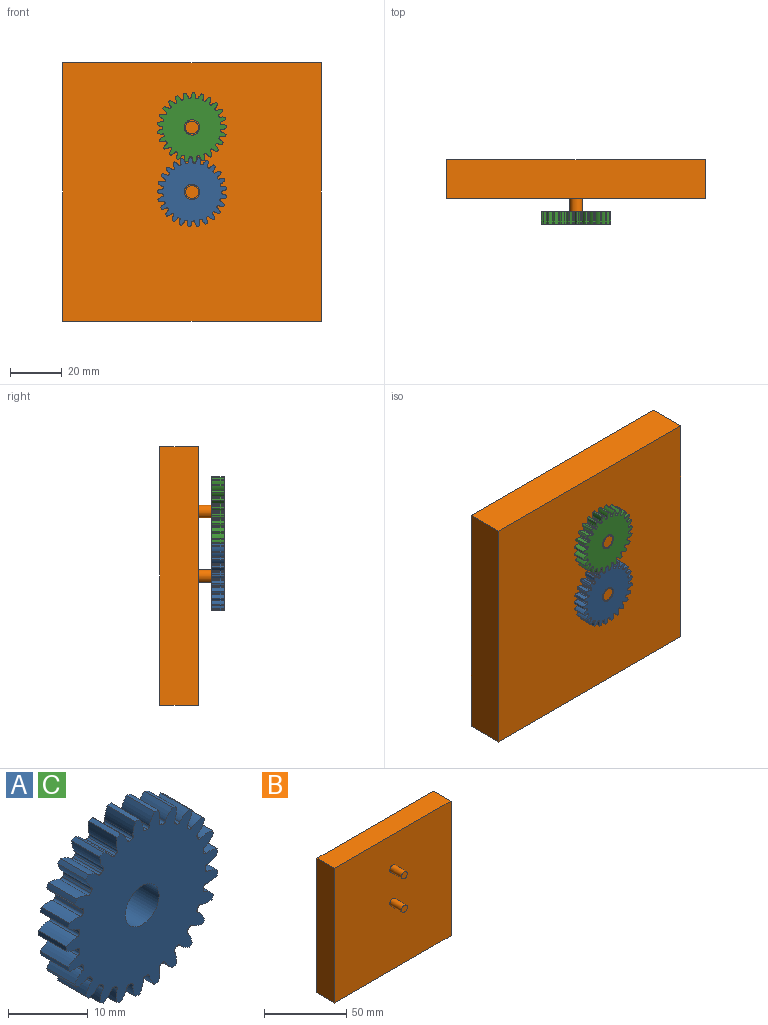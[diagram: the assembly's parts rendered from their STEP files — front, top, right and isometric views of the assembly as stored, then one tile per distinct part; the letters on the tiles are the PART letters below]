
ASSEMBLY  parts=3 mates=2
PART A: 153 faces, bbox 26.9x5x27 mm
  f0: extruded ~5x1.84mm, area 10.1mm2, adj f100,f101,f102,f103
  f1: cylinder r=11.25mm len=5mm, axis (0,1,0), area 1.9mm2, adj f101,f102,f103,f104
  f2: extruded ~5x1.84mm, area 10.1mm2, adj f3,f101,f102,f104
  f3: cylinder r=13.5mm len=5mm, axis (0,1,0), area 3.6mm2, adj f2,f4,f101,f102
  f4: extruded ~5x1.98mm, area 10.1mm2, adj f3,f101,f102,f105
  f5: cylinder r=11.25mm len=5mm, axis (0,1,0), area 1.9mm2, adj f101,f102,f105,f106
  f6: extruded ~5x1.59mm, area 10.1mm2, adj f7,f101,f102,f106
  f7: cylinder r=13.5mm len=5mm, axis (0,1,0), area 3.6mm2, adj f6,f8,f101,f102
  f8: extruded ~5x1.99mm, area 10.1mm2, adj f7,f101,f102,f107
  f9: cylinder r=11.25mm len=5mm, axis (0,1,0), area 1.9mm2, adj f101,f102,f107,f108
  f10: extruded ~5x1.57mm, area 10.1mm2, adj f11,f101,f102,f108
  f11: cylinder r=13.5mm len=5mm, axis (0,1,0), area 3.6mm2, adj f10,f12,f101,f102
  f12: extruded ~5x1.88mm, area 10.1mm2, adj f11,f101,f102,f109
  f13: cylinder r=11.25mm len=5mm, axis (0,1,0), area 1.9mm2, adj f101,f102,f109,f110
  f14: extruded ~5x1.83mm, area 10.1mm2, adj f15,f101,f102,f110
  f15: cylinder r=13.5mm len=5mm, axis (0,1,0), area 3.6mm2, adj f14,f16,f101,f102
  f16: extruded ~5x1.65mm, area 10.1mm2, adj f15,f101,f102,f111
  f17: cylinder r=11.25mm len=5mm, axis (0,1,0), area 1.9mm2, adj f101,f102,f111,f112
  f18: extruded ~5x1.97mm, area 10.1mm2, adj f19,f101,f102,f112
  f19: cylinder r=13.5mm len=5mm, axis (0,1,0), area 3.6mm2, adj f18,f20,f101,f102
  f20: extruded ~5x1.51mm, area 10.1mm2, adj f19,f101,f102,f113
  f21: cylinder r=11.25mm len=5mm, axis (0,1,0), area 1.9mm2, adj f101,f102,f113,f114
  f22: extruded ~5x1.99mm, area 10.1mm2, adj f23,f101,f102,f114
  f23: cylinder r=13.5mm len=5mm, axis (0,1,0), area 3.6mm2, adj f22,f24,f101,f102
  f24: extruded ~5x1.79mm, area 10.1mm2, adj f23,f101,f102,f115
  f25: cylinder r=11.25mm len=5mm, axis (0,1,0), area 1.9mm2, adj f101,f102,f115,f116
  f26: extruded ~5x1.89mm, area 10.1mm2, adj f27,f101,f102,f116
  f27: cylinder r=13.5mm len=5mm, axis (0,1,0), area 3.6mm2, adj f26,f28,f101,f102
  f28: extruded ~5x1.96mm, area 10.1mm2, adj f27,f101,f102,f117
  f29: cylinder r=11.25mm len=5mm, axis (0,1,0), area 1.9mm2, adj f101,f102,f117,f118
  f30: extruded ~5x1.67mm, area 10.1mm2, adj f31,f101,f102,f118
  f31: cylinder r=13.5mm len=5mm, axis (0,1,0), area 3.6mm2, adj f30,f32,f101,f102
  f32: extruded ~5x2mm, area 10.1mm2, adj f31,f101,f102,f119
  f33: cylinder r=11.25mm len=5mm, axis (0,1,0), area 1.9mm2, adj f101,f102,f119,f120
  f34: extruded ~5x1.49mm, area 10.1mm2, adj f35,f101,f102,f120
  f35: cylinder r=13.5mm len=5mm, axis (0,1,0), area 3.6mm2, adj f34,f36,f101,f102
  f36: extruded ~5x1.92mm, area 10.1mm2, adj f35,f101,f102,f121
  f37: cylinder r=11.25mm len=5mm, axis (0,1,0), area 1.9mm2, adj f101,f102,f121,f122
  f38: extruded ~5x1.78mm, area 10.1mm2, adj f39,f101,f102,f122
  f39: cylinder r=13.5mm len=5mm, axis (0,1,0), area 3.6mm2, adj f38,f40,f101,f102
  f40: extruded ~5x1.72mm, area 10.1mm2, adj f39,f101,f102,f123
  f41: cylinder r=11.25mm len=5mm, axis (0,1,0), area 1.9mm2, adj f101,f102,f123,f124
  f42: extruded ~5x1.95mm, area 10.1mm2, adj f43,f101,f102,f124
  f43: cylinder r=13.5mm len=5mm, axis (0,1,0), area 3.6mm2, adj f42,f44,f101,f102
  f44: extruded ~5x1.43mm, area 10.1mm2, adj f43,f101,f102,f125
  f45: cylinder r=11.25mm len=5mm, axis (0,1,0), area 1.9mm2, adj f101,f102,f125,f126
  f46: extruded ~5x2mm, area 10.1mm2, adj f47,f101,f102,f126
  f47: cylinder r=13.5mm len=5mm, axis (0,1,0), area 3.6mm2, adj f46,f48,f101,f102
  f48: extruded ~5x1.73mm, area 10.1mm2, adj f47,f101,f102,f127
  f49: cylinder r=11.25mm len=5mm, axis (0,1,0), area 1.9mm2, adj f101,f102,f127,f128
  f50: extruded ~5x1.93mm, area 10.1mm2, adj f51,f101,f102,f128
  f51: cylinder r=13.5mm len=5mm, axis (0,1,0), area 3.6mm2, adj f50,f52,f101,f102
  f52: extruded ~5x1.93mm, area 10.1mm2, adj f51,f101,f102,f129
  f53: cylinder r=11.25mm len=5mm, axis (0,1,0), area 1.9mm2, adj f101,f102,f129,f130
  f54: extruded ~5x1.73mm, area 10.1mm2, adj f55,f101,f102,f130
  f55: cylinder r=13.5mm len=5mm, axis (0,1,0), area 3.6mm2, adj f54,f56,f101,f102
  f56: extruded ~5x2mm, area 10.1mm2, adj f55,f101,f102,f131
  f57: cylinder r=11.25mm len=5mm, axis (0,1,0), area 1.9mm2, adj f101,f102,f131,f132
  f58: extruded ~5x1.43mm, area 10.1mm2, adj f59,f101,f102,f132
  f59: cylinder r=13.5mm len=5mm, axis (0,1,0), area 3.6mm2, adj f58,f60,f101,f102
  f60: extruded ~5x1.95mm, area 10.1mm2, adj f59,f101,f102,f133
  f61: cylinder r=11.25mm len=5mm, axis (0,1,0), area 1.9mm2, adj f101,f102,f133,f134
  f62: extruded ~5x1.72mm, area 10.1mm2, adj f63,f101,f102,f134
  f63: cylinder r=13.5mm len=5mm, axis (0,1,0), area 3.6mm2, adj f62,f64,f101,f102
  f64: extruded ~5x1.78mm, area 10.1mm2, adj f63,f101,f102,f135
  f65: cylinder r=11.25mm len=5mm, axis (0,1,0), area 1.9mm2, adj f101,f102,f135,f136
  f66: extruded ~5x1.92mm, area 10.1mm2, adj f67,f101,f102,f136
  f67: cylinder r=13.5mm len=5mm, axis (0,1,0), area 3.6mm2, adj f66,f68,f101,f102
  f68: extruded ~5x1.49mm, area 10.1mm2, adj f67,f101,f102,f137
  f69: cylinder r=11.25mm len=5mm, axis (0,1,0), area 1.9mm2, adj f101,f102,f137,f138
  f70: extruded ~5x2mm, area 10.1mm2, adj f71,f101,f102,f138
  f71: cylinder r=13.5mm len=5mm, axis (0,1,0), area 3.6mm2, adj f70,f72,f101,f102
  f72: extruded ~5x1.67mm, area 10.1mm2, adj f71,f101,f102,f139
  f73: cylinder r=11.25mm len=5mm, axis (0,1,0), area 1.9mm2, adj f101,f102,f139,f140
  f74: extruded ~5x1.96mm, area 10.1mm2, adj f75,f101,f102,f140
  f75: cylinder r=13.5mm len=5mm, axis (0,1,0), area 3.6mm2, adj f74,f76,f101,f102
  f76: extruded ~5x1.89mm, area 10.1mm2, adj f75,f101,f102,f141
  f77: cylinder r=11.25mm len=5mm, axis (0,1,0), area 1.9mm2, adj f101,f102,f141,f142
  f78: extruded ~5x1.79mm, area 10.1mm2, adj f79,f101,f102,f142
  f79: cylinder r=13.5mm len=5mm, axis (0,1,0), area 3.6mm2, adj f78,f80,f101,f102
  f80: extruded ~5x1.99mm, area 10.1mm2, adj f79,f101,f102,f143
  f81: cylinder r=11.25mm len=5mm, axis (0,1,0), area 1.9mm2, adj f101,f102,f143,f144
  f82: extruded ~5x1.51mm, area 10.1mm2, adj f83,f101,f102,f144
  f83: cylinder r=13.5mm len=5mm, axis (0,1,0), area 3.6mm2, adj f82,f84,f101,f102
  f84: extruded ~5x1.97mm, area 10.1mm2, adj f83,f101,f102,f145
  f85: cylinder r=11.25mm len=5mm, axis (0,1,0), area 1.9mm2, adj f101,f102,f145,f146
  f86: extruded ~5x1.65mm, area 10.1mm2, adj f87,f101,f102,f146
  f87: cylinder r=13.5mm len=5mm, axis (0,1,0), area 3.6mm2, adj f86,f88,f101,f102
  f88: extruded ~5x1.83mm, area 10.1mm2, adj f87,f101,f102,f147
  f89: cylinder r=11.25mm len=5mm, axis (0,1,0), area 1.9mm2, adj f101,f102,f147,f148
  f90: extruded ~5x1.88mm, area 10.1mm2, adj f91,f101,f102,f148
  f91: cylinder r=13.5mm len=5mm, axis (0,1,0), area 3.6mm2, adj f90,f92,f101,f102
  f92: extruded ~5x1.57mm, area 10.1mm2, adj f91,f101,f102,f149
  f93: cylinder r=11.25mm len=5mm, axis (0,1,0), area 1.9mm2, adj f101,f102,f149,f150
  f94: extruded ~5x1.99mm, area 10.1mm2, adj f95,f101,f102,f150
  f95: cylinder r=13.5mm len=5mm, axis (0,1,0), area 3.6mm2, adj f94,f96,f101,f102
  f96: extruded ~5x1.59mm, area 10.1mm2, adj f95,f101,f102,f151
  f97: cylinder r=11.25mm len=5mm, axis (0,1,0), area 1.9mm2, adj f101,f102,f151,f152
  f98: extruded ~5x1.98mm, area 10.1mm2, adj f100,f101,f102,f152
  f99: cylinder r=3mm len=6mm, axis (0,1,0), area 94.2mm2, adj f101,f102
  f100: cylinder r=13.5mm len=5mm, axis (0,1,0), area 3.6mm2, adj f0,f98,f101,f102
  f101: plane 26.99x26.94mm, normal (0,-1,0), area 455.2mm2, adj f0,f1,f2,f3,f4,f5,f6,f7
  f102: plane 26.99x26.94mm, normal (0,1,0), area 455.2mm2, adj f0,f1,f2,f3,f4,f5,f6,f7
  f103: cylinder r=0.36mm len=5mm, axis (0,1,0), area 2.8mm2, adj f0,f1,f101,f102
  f104: cylinder r=0.36mm len=5mm, axis (0,1,0), area 2.8mm2, adj f1,f2,f101,f102
  f105: cylinder r=0.36mm len=5mm, axis (0,1,0), area 2.8mm2, adj f4,f5,f101,f102
  f106: cylinder r=0.36mm len=5mm, axis (0,1,0), area 2.8mm2, adj f5,f6,f101,f102
  f107: cylinder r=0.36mm len=5mm, axis (0,1,0), area 2.8mm2, adj f8,f9,f101,f102
  f108: cylinder r=0.36mm len=5mm, axis (0,1,0), area 2.8mm2, adj f9,f10,f101,f102
  f109: cylinder r=0.36mm len=5mm, axis (0,1,0), area 2.8mm2, adj f12,f13,f101,f102
  f110: cylinder r=0.36mm len=5mm, axis (0,1,0), area 2.8mm2, adj f13,f14,f101,f102
  f111: cylinder r=0.36mm len=5mm, axis (0,1,0), area 2.8mm2, adj f16,f17,f101,f102
  f112: cylinder r=0.36mm len=5mm, axis (0,1,0), area 2.8mm2, adj f17,f18,f101,f102
  f113: cylinder r=0.36mm len=5mm, axis (0,1,0), area 2.8mm2, adj f20,f21,f101,f102
  f114: cylinder r=0.36mm len=5mm, axis (0,1,0), area 2.8mm2, adj f21,f22,f101,f102
  f115: cylinder r=0.36mm len=5mm, axis (0,1,0), area 2.8mm2, adj f24,f25,f101,f102
  f116: cylinder r=0.36mm len=5mm, axis (0,1,0), area 2.8mm2, adj f25,f26,f101,f102
  f117: cylinder r=0.36mm len=5mm, axis (0,1,0), area 2.8mm2, adj f28,f29,f101,f102
  f118: cylinder r=0.36mm len=5mm, axis (0,1,0), area 2.8mm2, adj f29,f30,f101,f102
  f119: cylinder r=0.36mm len=5mm, axis (0,1,0), area 2.8mm2, adj f32,f33,f101,f102
  f120: cylinder r=0.36mm len=5mm, axis (0,1,0), area 2.8mm2, adj f33,f34,f101,f102
  f121: cylinder r=0.36mm len=5mm, axis (0,1,0), area 2.8mm2, adj f36,f37,f101,f102
  f122: cylinder r=0.36mm len=5mm, axis (0,1,0), area 2.8mm2, adj f37,f38,f101,f102
  f123: cylinder r=0.36mm len=5mm, axis (0,1,0), area 2.8mm2, adj f40,f41,f101,f102
  f124: cylinder r=0.36mm len=5mm, axis (0,1,0), area 2.8mm2, adj f41,f42,f101,f102
  f125: cylinder r=0.36mm len=5mm, axis (0,1,0), area 2.8mm2, adj f44,f45,f101,f102
  f126: cylinder r=0.36mm len=5mm, axis (0,1,0), area 2.8mm2, adj f45,f46,f101,f102
  f127: cylinder r=0.36mm len=5mm, axis (0,1,0), area 2.8mm2, adj f48,f49,f101,f102
  f128: cylinder r=0.36mm len=5mm, axis (0,1,0), area 2.8mm2, adj f49,f50,f101,f102
  f129: cylinder r=0.36mm len=5mm, axis (0,1,0), area 2.8mm2, adj f52,f53,f101,f102
  f130: cylinder r=0.36mm len=5mm, axis (0,1,0), area 2.8mm2, adj f53,f54,f101,f102
  f131: cylinder r=0.36mm len=5mm, axis (0,1,0), area 2.8mm2, adj f56,f57,f101,f102
  f132: cylinder r=0.36mm len=5mm, axis (0,1,0), area 2.8mm2, adj f57,f58,f101,f102
  f133: cylinder r=0.36mm len=5mm, axis (0,1,0), area 2.8mm2, adj f60,f61,f101,f102
  f134: cylinder r=0.36mm len=5mm, axis (0,1,0), area 2.8mm2, adj f61,f62,f101,f102
  f135: cylinder r=0.36mm len=5mm, axis (0,1,0), area 2.8mm2, adj f64,f65,f101,f102
  f136: cylinder r=0.36mm len=5mm, axis (0,1,0), area 2.8mm2, adj f65,f66,f101,f102
  f137: cylinder r=0.36mm len=5mm, axis (0,1,0), area 2.8mm2, adj f68,f69,f101,f102
  f138: cylinder r=0.36mm len=5mm, axis (0,1,0), area 2.8mm2, adj f69,f70,f101,f102
  f139: cylinder r=0.36mm len=5mm, axis (0,1,0), area 2.8mm2, adj f72,f73,f101,f102
  f140: cylinder r=0.36mm len=5mm, axis (0,1,0), area 2.8mm2, adj f73,f74,f101,f102
  f141: cylinder r=0.36mm len=5mm, axis (0,1,0), area 2.8mm2, adj f76,f77,f101,f102
  f142: cylinder r=0.36mm len=5mm, axis (0,1,0), area 2.8mm2, adj f77,f78,f101,f102
  f143: cylinder r=0.36mm len=5mm, axis (0,1,0), area 2.8mm2, adj f80,f81,f101,f102
  f144: cylinder r=0.36mm len=5mm, axis (0,1,0), area 2.8mm2, adj f81,f82,f101,f102
  f145: cylinder r=0.36mm len=5mm, axis (0,1,0), area 2.8mm2, adj f84,f85,f101,f102
  f146: cylinder r=0.36mm len=5mm, axis (0,1,0), area 2.8mm2, adj f85,f86,f101,f102
  f147: cylinder r=0.36mm len=5mm, axis (0,1,0), area 2.8mm2, adj f88,f89,f101,f102
  f148: cylinder r=0.36mm len=5mm, axis (0,1,0), area 2.8mm2, adj f89,f90,f101,f102
  f149: cylinder r=0.36mm len=5mm, axis (0,1,0), area 2.8mm2, adj f92,f93,f101,f102
  f150: cylinder r=0.36mm len=5mm, axis (0,1,0), area 2.8mm2, adj f93,f94,f101,f102
  f151: cylinder r=0.36mm len=5mm, axis (0,1,0), area 2.8mm2, adj f96,f97,f101,f102
  f152: cylinder r=0.36mm len=5mm, axis (0,1,0), area 2.8mm2, adj f97,f98,f101,f102
PART B: 10 faces, bbox 100x25x100 mm
  f0: plane 100x15mm, normal (0,0,-1), area 1500mm2, adj f1,f3,f4,f5
  f1: plane 100x15mm, normal (1,0,0), area 1500mm2, adj f0,f2,f4,f5
  f2: plane 100x15mm, normal (0,0,1), area 1500mm2, adj f1,f3,f4,f5
  f3: plane 100x15mm, normal (-1,0,0), area 1500mm2, adj f0,f2,f4,f5
  f4: plane 100x100mm, normal (0,1,0), area 10000mm2, adj f0,f1,f2,f3
  f5: plane 100x100mm, normal (0,-1,0), area 9960.7mm2, adj f0,f1,f2,f3,f6,f8
  f6: cylinder r=2.5mm len=10mm, axis (0,1,0), area 157.1mm2, adj f5,f7
  f7: plane 5x5mm, normal (0,-1,0), area 19.6mm2, adj f6
  f8: cylinder r=2.5mm len=10mm, axis (0,1,0), area 157.1mm2, adj f5,f9
  f9: plane 5x5mm, normal (0,-1,0), area 19.6mm2, adj f8
PART C: same geometry as A
PLACE A rot(axis=(0,-1,0),99.9deg) t=(3.94,1.39,6.64)mm
PLACE B t=(3.94,6.39,6.64)mm fixed
PLACE C rot(axis=(0,-1,0),80.1deg) t=(3.94,1.39,31.64)mm
MATE revolute A.f3 <-> B.f6  axis (0,-1,0) through (3.94,-3.61,6.64)mm
MATE revolute C.f3 <-> B.f8  axis (0,-1,0) through (3.94,-3.61,31.64)mm
